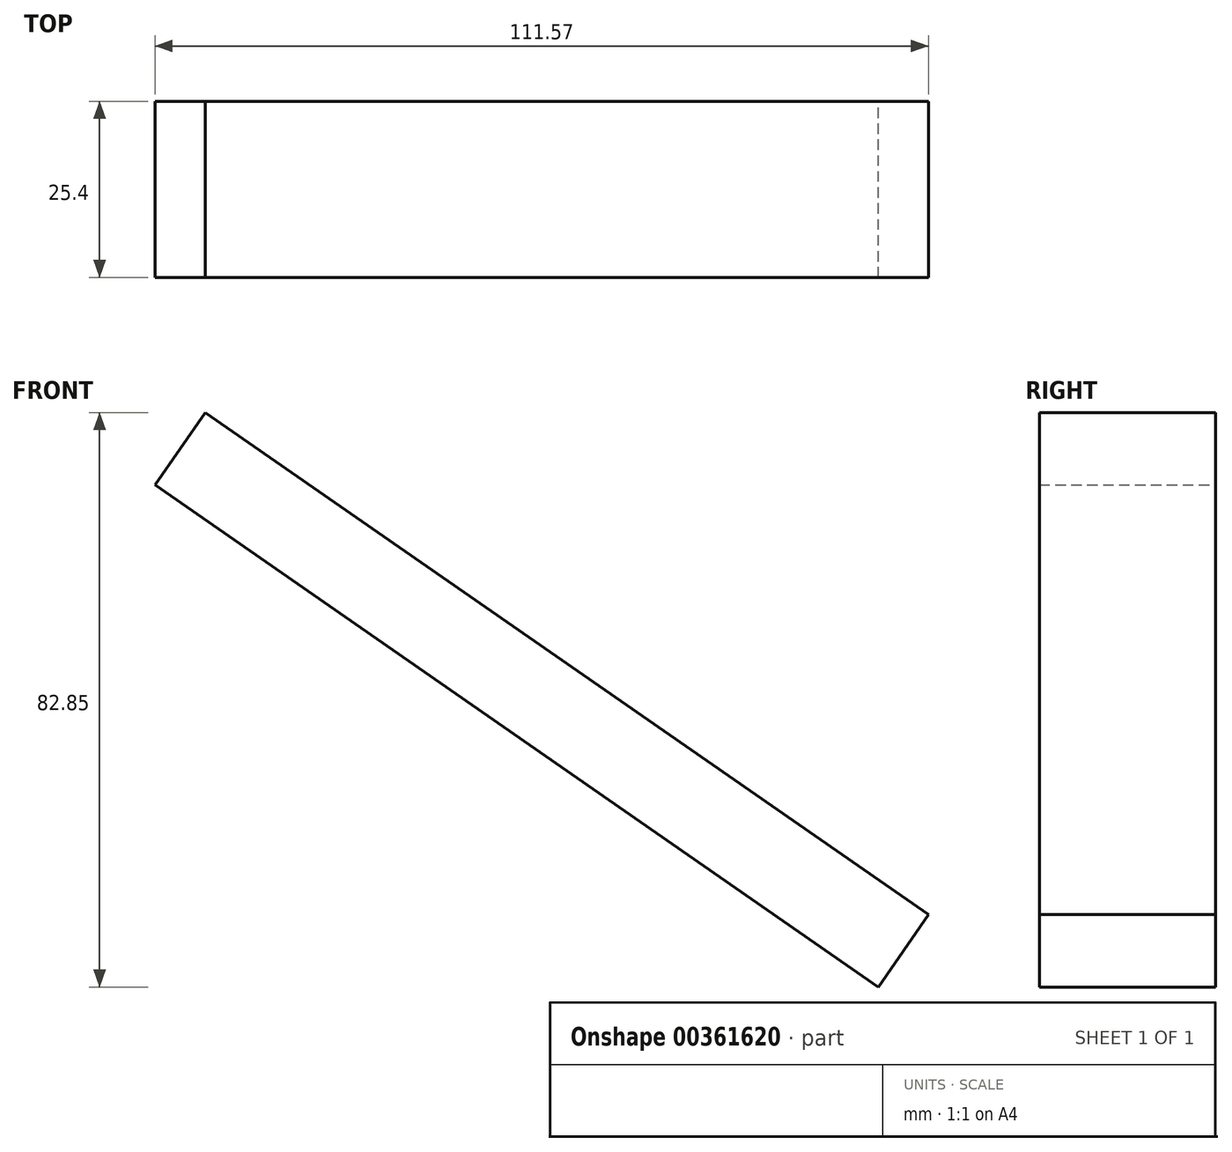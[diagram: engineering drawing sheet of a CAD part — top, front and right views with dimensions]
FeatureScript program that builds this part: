
annotation { "Feature Type Name" : "Feature", "Feature Type Description" : "" }
export const myFeature = defineFeature(function(context is Context, id is Id, definition is map)
    precondition{}
    {
        {
            var Q0;
            Q0=qCreatedBy(makeId("Front.planeOp"),FACE);
            var sketch = newSketch(context, id + "F0", { "sketchPlane" : qUnion([Q0])});
            skLineSegment(sketch, "E0", {"start": v(-77.5, 44.08) * mm, "end": v(26.83, -28.33) * mm});
            skLineSegment(sketch, "E1", {"start": v(-84.74, 33.65) * mm, "end": v(19.6, -38.77) * mm});
            skLineSegment(sketch, "E2", {"start": v(-84.74, 33.65) * mm, "end": v(-77.5, 44.08) * mm});
            skLineSegment(sketch, "E3", {"start": v(26.83, -28.33) * mm, "end": v(19.6, -38.77) * mm});
            skLineSegment(sketch, "E4.MirrorCS", {"start": v(26.83, 33.65) * mm, "end": v(-77.5, -38.77) * mm});
            skLineSegment(sketch, "E5.MirrorCS", {"start": v(19.6, 44.08) * mm, "end": v(-84.74, -28.33) * mm});
            skLineSegment(sketch, "E6.MirrorCS", {"start": v(26.83, 33.65) * mm, "end": v(19.6, 44.08) * mm});
            skLineSegment(sketch, "E7.MirrorCS", {"start": v(-84.74, -28.33) * mm, "end": v(-77.5, -38.77) * mm});
            skSolve(sketch);
        }
        {
            var Q0;
            {var subQ0=sQuery(id+"F0.wireOp",EDGE,"E2");Q0=makeQuery(id+"F0.imprint","IMPRINT",FACE,{"disambiguationData":[TD([[makeQuery(id+"F0.imprint","IMPRINT",EDGE,{"derivedFrom":subQ0}),-1.0]])]});}
            var Q1;
            {var subQ0=sQuery(id+"F0.wireOp",EDGE,"E5.MirrorCS");var subQ1=sQuery(id+"F0.wireOp",EDGE,"E0");var subQ2=makeQuery(id+"F0.imprint","INTERSECT",VERTEX,{"derivedFrom":[subQ1,subQ0]});Q1=makeQuery(id+"F0.imprint","IMPRINT",FACE,{"disambiguationData":[TD([[makeQuery(id+"F0.imprint","IMPRINT",EDGE,{"disambiguationData":[TD([[subQ2,-1.0]])],"derivedFrom":subQ1}),-1.0]])]});}
            var Q2;
            {var subQ0=sQuery(id+"F0.wireOp",EDGE,"E3");Q2=makeQuery(id+"F0.imprint","IMPRINT",FACE,{"disambiguationData":[TD([[makeQuery(id+"F0.imprint","IMPRINT",EDGE,{"derivedFrom":subQ0}),-1.0]])]});}
            extrude(context, id + "F1", {"entities" : qUnion([Q0, Q1, Q2]), "depth" : 25.4 * mm});
        }
    });
